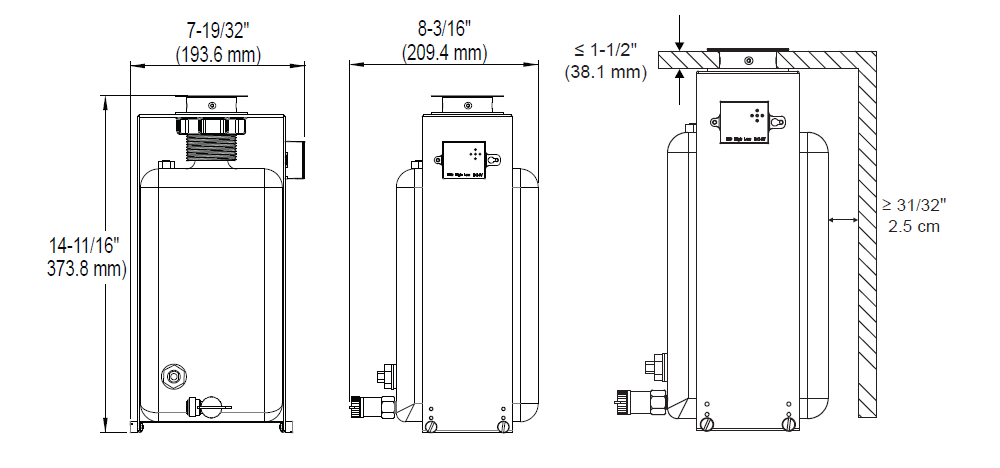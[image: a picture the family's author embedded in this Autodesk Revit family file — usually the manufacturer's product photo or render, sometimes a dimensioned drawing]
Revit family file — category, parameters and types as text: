
# Revit family: Soap_Dispenser-Bobrick-B-820_Series
name_source: partatom
category: Specialty Equipment
units: mm (PartAtom-declared; Revit-internal decimal feet)

## family parameters
Always vertical = No
Cut with Voids When Loaded = No
OmniClass Number = 23.40.20.21.34
OmniClass Title = Soap Holders, Dispensers
Part Type = Normal
Room Calculation Point = No
Round Connector Dimension = Use Diameter
Shared = Yes
Work Plane-Based = Yes

## types (2) — shared parameters
6V AC Adapter 3974-58 = No
6V AC Adapter 824-241 = No
Assembly Code = C1030200
B-820 (Multi-Feed Soap Reservoir Tank) = Yes
Capacity = 1.6 gal (6.0 L)
Contertop Thickness = 1"
Contertop Thickness Constraint = 1"
Default Elevation = 0"
Description = AUTOMATIC, TOP-FILL, MULTI-FEED BULK SOAP DISPENSER SYSTEM
Dispenser 1 = Yes
Dispenser 2 = Yes
Dispenser 3 = Yes
Dispenser 4 = Yes
Dispenser 5 = Yes
Dispenser 6 = Yes
Distance between Dispensers = 43 5/16"
Distance between Dispensers Constraint = 43 5/16"
Height = 3 29/32"
Installation Type = Deck Mounted
Manufacturer = Bobrick
Material = Stainkess Steel-Bobrick-Polished
Min. Clearanace to back of Wall = 1 3/8"
Soap Reservoir Tank Material = Polypropylene-Bobrick-Black
Spout and Stem Assembly Material = Stainkess Steel-Bobrick-Polished
Tube Length = 6"
Tube Length Constraint = 6"
URL = https://www.bobrick.com
Width = 1 11/16"

## per-type parameters (varying)
| type | Type Comments | Type of Dispenser |
| B-820-258 | Liquid Soap Pump | B-820 : B-820-258 |
| B-820-248 | Foam Soap Pump | B-820 : B-820-248 |

note: column(s) folded — value = type name in every type: Model

## geometry (parser evidence)
native form markers: Sweep x9
no freeform markers — native parametric forms only
